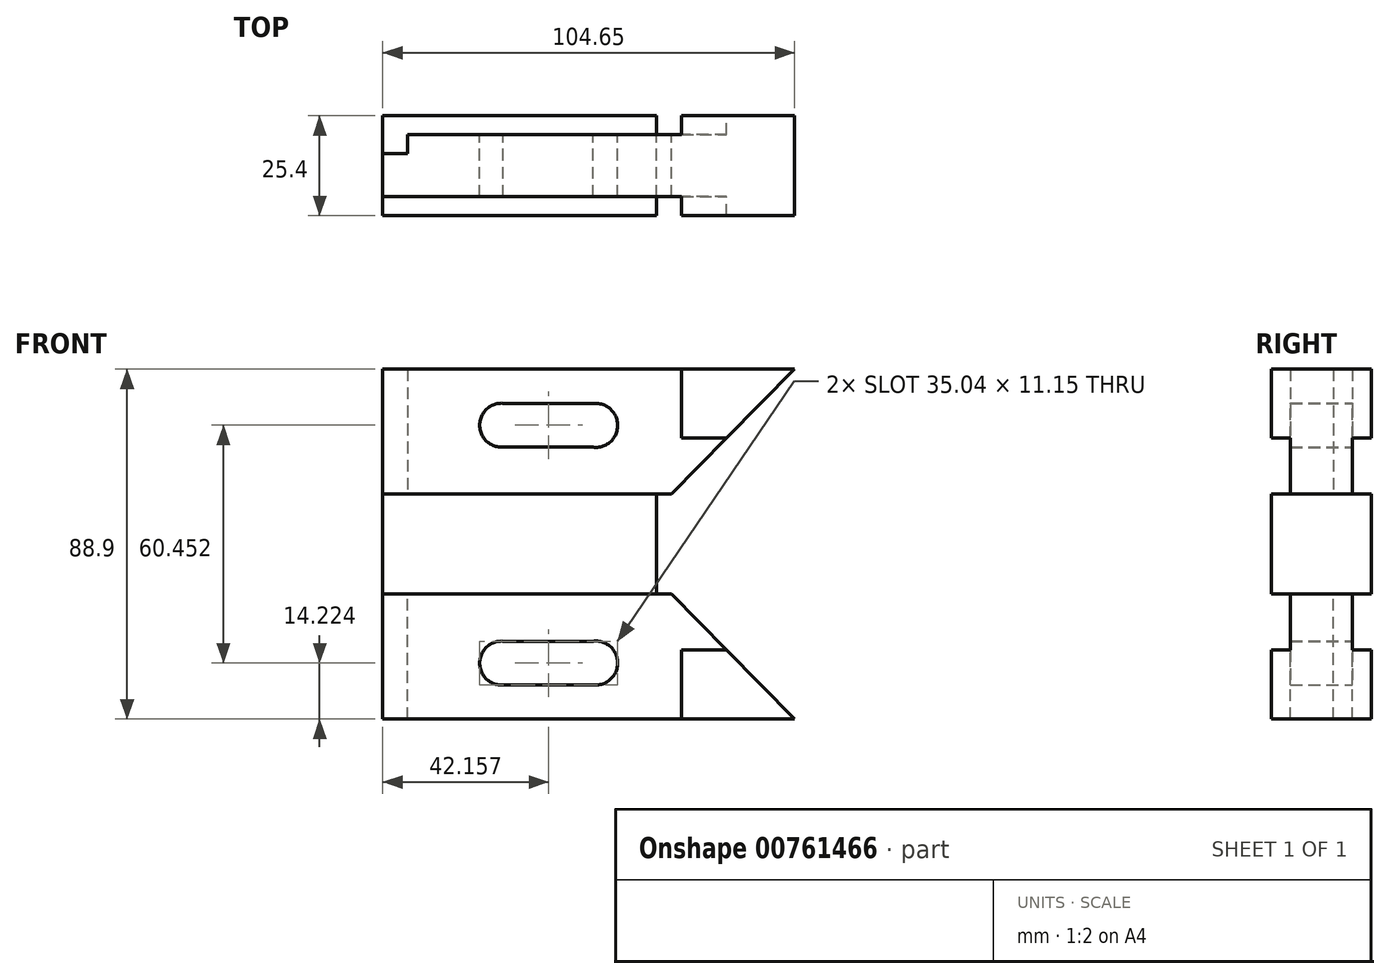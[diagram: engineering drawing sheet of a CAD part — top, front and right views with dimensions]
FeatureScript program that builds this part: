
annotation { "Feature Type Name" : "Feature", "Feature Type Description" : "" }
export const myFeature = defineFeature(function(context is Context, id is Id, definition is map)
    precondition{}
    {
        {
            var Q0;
            Q0=qCreatedBy(makeId("Front.planeOp"),FACE);
            var sketch = newSketch(context, id + "F0", { "sketchPlane" : qUnion([Q0])});
            skLineSegment(sketch, "E0.bottom", {"start": v(-60.52, 44.45) * mm, "end": v(44.13, 44.45) * mm});
            skLineSegment(sketch, "E0.top", {"start": v(-60.52, 12.7) * mm, "end": v(12.8, 12.7) * mm});
            skLineSegment(sketch, "E0.left", {"start": v(-60.52, 44.45) * mm, "end": v(-60.52, 12.7) * mm});
            skLineSegment(sketch, "E1.bottom", {"start": v(-54.17, 44.45) * mm, "end": v(15.43, 44.45) * mm});
            skLineSegment(sketch, "E1.top", {"start": v(-54.17, 12.7) * mm, "end": v(12.8, 12.7) * mm});
            skLineSegment(sketch, "E1.left", {"start": v(-54.17, 44.45) * mm, "end": v(-54.17, 12.7) * mm});
            skLineSegment(sketch, "E1.right", {"start": v(15.43, 44.45) * mm, "end": v(15.43, 26.92) * mm});
            skLineSegment(sketch, "E2.bottom", {"start": v(15.43, 44.45) * mm, "end": v(44.13, 44.45) * mm});
            skArc(sketch, "E3", {"start": v(-29.91, 35.8) * mm, "mid": v(-35.88, 30.23) * mm, "end": v(-29.91, 24.65) * mm});
            skArc(sketch, "E4", {"start": v(-7.13, 24.65) * mm, "mid": v(-0.84, 29.83) * mm, "end": v(-6.41, 35.78) * mm});
            skLineSegment(sketch, "E5", {"start": v(-29.91, 24.65) * mm, "end": v(-6.87, 24.65) * mm});
            skLineSegment(sketch, "E6", {"start": v(-29.91, 35.8) * mm, "end": v(-6.41, 35.78) * mm});
            skLineSegment(sketch, "E7", {"start": v(15.43, 26.92) * mm, "end": v(26.83, 26.92) * mm});
            skLineSegment(sketch, "E8", {"start": v(44.13, 44.45) * mm, "end": v(12.8, 12.7) * mm});
            skLineSegment(sketch, "E9.bottom", {"start": v(-60.52, 12.7) * mm, "end": v(8.99, 12.7) * mm});
            skLineSegment(sketch, "E9.top", {"start": v(-60.52, 0) * mm, "end": v(8.99, 0) * mm});
            skLineSegment(sketch, "E9.left", {"start": v(-60.52, 12.7) * mm, "end": v(-60.52, 0) * mm});
            skLineSegment(sketch, "E9.right", {"start": v(8.99, 12.7) * mm, "end": v(8.99, 0) * mm});
            skLineSegment(sketch, "E10", {"start": v(44.13, 44.45) * mm, "end": v(44.13, 12.77) * mm});
            skLineSegment(sketch, "E11", {"start": v(44.13, 12.77) * mm, "end": v(12.8, 12.7) * mm});
            skSolve(sketch);
        }
        {
            var Q0;
            Q0=makeQuery(id+"F0.imprint","IMPRINT",FACE,{"disambiguationData":[TD([[makeQuery(id+"F0.imprint","IMPRINT",EDGE,{"derivedFrom":sQuery(id+"F0.wireOp",EDGE,"E9.top")}),1.0]])]});
            var Q1;
            {var subQ0=sQuery(id+"F0.wireOp",EDGE,"E1.right");Q1=makeQuery(id+"F0.imprint","IMPRINT",FACE,{"disambiguationData":[TD([[makeQuery(id+"F0.imprint","IMPRINT",EDGE,{"derivedFrom":subQ0}),1.0]])]});}
            extrude(context, id + "F1", {"entities" : qUnion([Q0, Q1]), "endBound" : BoundingType.SYMMETRIC, "depth" : 25.4 * mm, "offsetDistance" : 25.4 * mm});
        }
        {
            var Q0;
            {var subQ5=sQuery(id+"F0.wireOp",EDGE,"E1.left");Q0=makeQuery(id+"F0.imprint","IMPRINT",FACE,{"disambiguationData":[TD([[makeQuery(id+"F0.imprint","IMPRINT",EDGE,{"derivedFrom":subQ5}),1.0]])]});}
            extrude(context, id + "F2", {"entities" : qUnion([Q0]), "endBound" : BoundingType.SYMMETRIC, "depth" : 15.75 * mm, "offsetDistance" : 25.4 * mm});
        }
        {
            var Q0;
            {var subQ2=sQuery(id+"F0.wireOp",EDGE,"E0.left");Q0=makeQuery(id+"F0.imprint","IMPRINT",FACE,{"disambiguationData":[TD([[makeQuery(id+"F0.imprint","IMPRINT",EDGE,{"derivedFrom":subQ2}),1.0]])]});}
            extrude(context, id + "F3", {"entities" : qUnion([Q0]), "depth" : 7.87 * mm, "offsetDistance" : 25.4 * mm, "hasSecondDirection" : true, "secondDirectionOppositeDirection" : true, "secondDirectionDepth" : 3.05 * mm});
        }
        {
            var Q0;
            Q0=makeQuery(id+"F2.opExtrude","SWEPT_BODY",BODY,{"disambiguationData":[OSD([sQuery(id+"F0.wireOp",EDGE,"E0.bottom"),sQuery(id+"F0.wireOp",EDGE,"E0.top"),sQuery(id+"F0.wireOp",EDGE,"E1.left"),sQuery(id+"F0.wireOp",EDGE,"E1.right"),sQuery(id+"F0.wireOp",EDGE,"E3"),sQuery(id+"F0.wireOp",EDGE,"E4"),sQuery(id+"F0.wireOp",EDGE,"E5"),sQuery(id+"F0.wireOp",EDGE,"E6"),sQuery(id+"F0.wireOp",EDGE,"E7"),sQuery(id+"F0.wireOp",EDGE,"E8")])]});
            var Q1;
            Q1=makeQuery(id+"F1.opExtrude","SWEPT_BODY",BODY,{"disambiguationData":[OSD([sQuery(id+"F0.wireOp",EDGE,"E0.top"),sQuery(id+"F0.wireOp",EDGE,"E9.top"),sQuery(id+"F0.wireOp",EDGE,"E9.left"),sQuery(id+"F0.wireOp",EDGE,"E9.right")])]});
            var Q2;
            Q2=makeQuery(id+"F1.opExtrude","SWEPT_BODY",BODY,{"disambiguationData":[OSD([sQuery(id+"F0.wireOp",EDGE,"E0.bottom"),sQuery(id+"F0.wireOp",EDGE,"E1.right"),sQuery(id+"F0.wireOp",EDGE,"E7"),sQuery(id+"F0.wireOp",EDGE,"E8")])]});
            var Q3;
            Q3=makeQuery(id+"F3.opExtrude","SWEPT_BODY",BODY,{"disambiguationData":[OSD([sQuery(id+"F0.wireOp",EDGE,"E0.bottom"),sQuery(id+"F0.wireOp",EDGE,"E0.top"),sQuery(id+"F0.wireOp",EDGE,"E0.left"),sQuery(id+"F0.wireOp",EDGE,"E1.left")])]});
            var Q4;
            Q4=qCreatedBy(makeId("Top.planeOp"),FACE);
            mirror(context, id + "F4", {"operationType" : NewBodyOperationType.ADD, "entities" : qUnion([Q0, Q1, Q2, Q3]), "mirrorPlane" : qUnion([Q4])});
        }
    });
